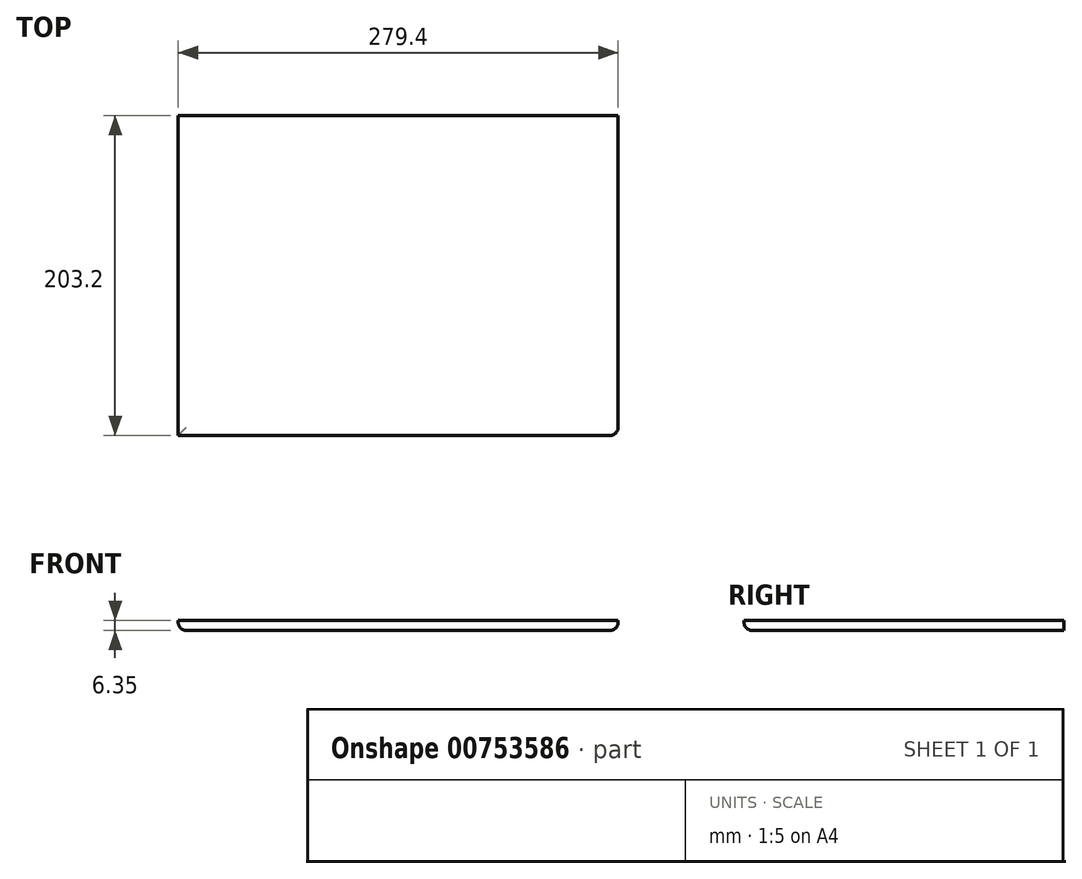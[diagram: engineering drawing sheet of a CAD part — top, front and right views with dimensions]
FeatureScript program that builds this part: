
annotation { "Feature Type Name" : "Feature", "Feature Type Description" : "" }
export const myFeature = defineFeature(function(context is Context, id is Id, definition is map)
    precondition{}
    {
        {
            var Q0;
            Q0=qCreatedBy(makeId("Top.planeOp"),FACE);
            var sketch = newSketch(context, id + "F0", { "sketchPlane" : qUnion([Q0])});
            skLineSegment(sketch, "E0.bottom", {"start": v(0, 0) * mm, "end": v(279.4, 0) * mm});
            skLineSegment(sketch, "E0.top", {"start": v(0, -203.2) * mm, "end": v(279.4, -203.2) * mm});
            skLineSegment(sketch, "E0.left", {"start": v(0, 0) * mm, "end": v(0, -203.2) * mm});
            skLineSegment(sketch, "E0.right", {"start": v(279.4, 0) * mm, "end": v(279.4, -203.2) * mm});
            skSolve(sketch);
        }
        {
            var Q0;
            Q0=makeQuery(id+"F0.imprint","IMPRINT",FACE,{"disambiguationData":[TD([[makeQuery(id+"F0.imprint","IMPRINT",EDGE,{"derivedFrom":sQuery(id+"F0.wireOp",EDGE,"E0.bottom")}),-1.0]])]});
            extrude(context, id + "F1", {"entities" : qUnion([Q0]), "depth" : 6.35 * mm, "offsetDistance" : 25.4 * mm});
        }
        {
            var Q0;
            Q0=makeQuery(id+"F1.opExtrude","CAP_EDGE",EDGE,{"disambiguationData":[OSD([sQuery(id+"F0.wireOp",EDGE,"E0.top")])],"isStart":true});
            var Q1;
            Q1=makeQuery(id+"F1.opExtrude","CAP_EDGE",EDGE,{"disambiguationData":[OSD([sQuery(id+"F0.wireOp",EDGE,"E0.left")])],"isStart":true});
            fillet(context, id + "F2", {"entities" : qUnion([Q0, Q1]), "radius" : 5.08 * mm, "tangentPropagation" : true, "allowEdgeOverflow" : false});
        }
        {
            var Q0;
            Q0=makeQuery(id+"F1.opExtrude","CAP_EDGE",EDGE,{"disambiguationData":[OSD([sQuery(id+"F0.wireOp",EDGE,"E0.right")])],"isStart":true});
            fillet(context, id + "F3", {"entities" : qUnion([Q0]), "radius" : 5.08 * mm, "tangentPropagation" : true, "allowEdgeOverflow" : false});
        }
    });
